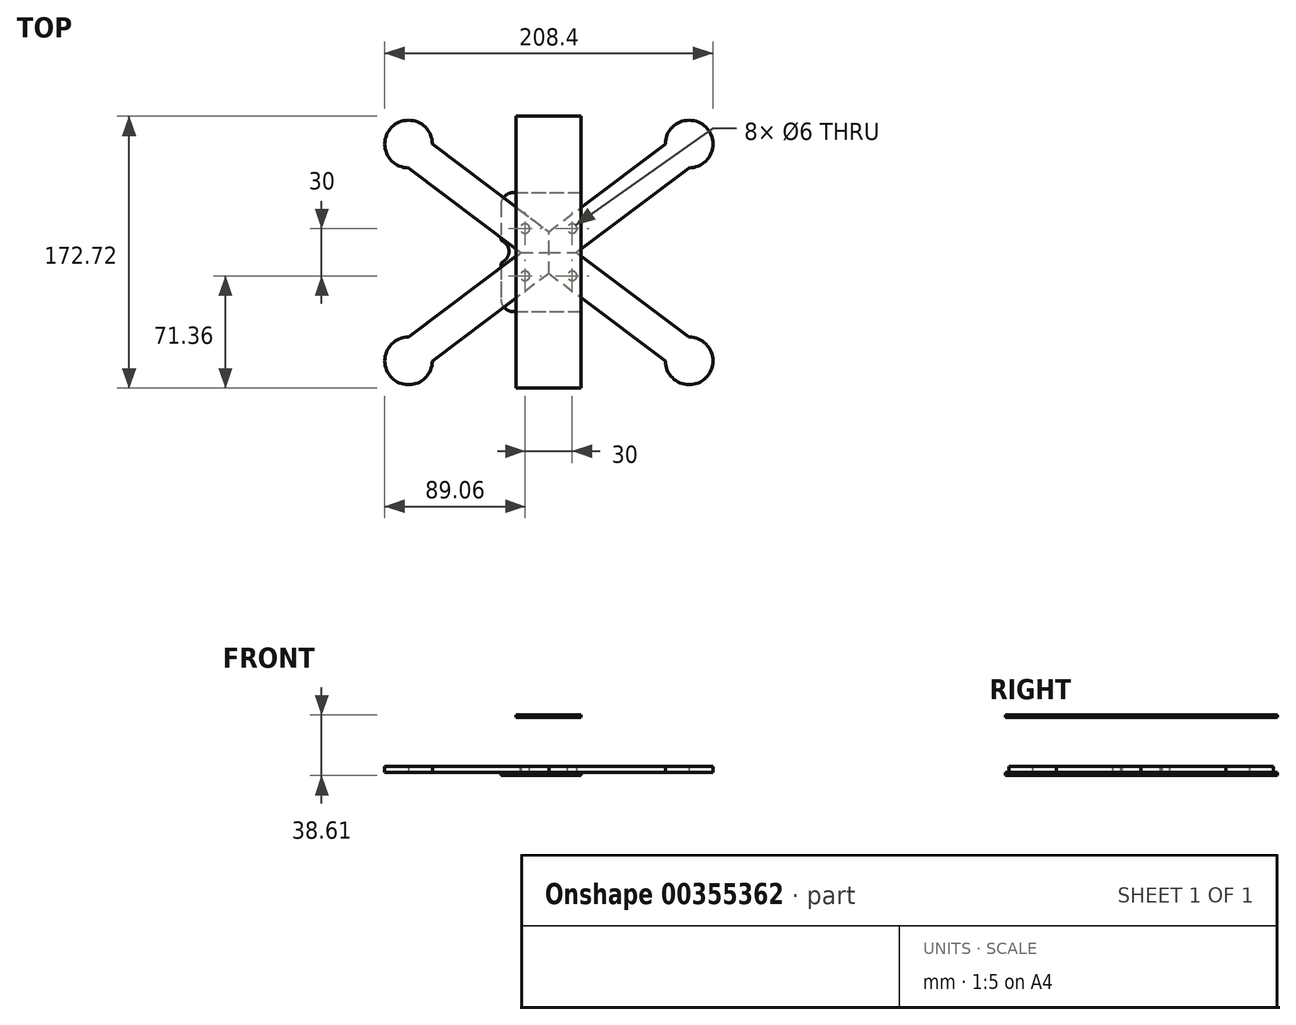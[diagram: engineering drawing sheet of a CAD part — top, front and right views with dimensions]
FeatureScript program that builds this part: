
annotation { "Feature Type Name" : "Feature", "Feature Type Description" : "" }
export const myFeature = defineFeature(function(context is Context, id is Id, definition is map)
    precondition{}
    {
        {
            var Q0;
            Q0=qCreatedBy(makeId("Top.planeOp"),FACE);
            var sketch = newSketch(context, id + "F0", { "sketchPlane" : qUnion([Q0])});
            skLineSegment(sketch, "E0.bottom", {"start": v(-20.57, 86.36) * mm, "end": v(20.58, 86.36) * mm});
            skLineSegment(sketch, "E0.top", {"start": v(-20.58, -86.36) * mm, "end": v(20.57, -86.36) * mm});
            skLineSegment(sketch, "E0.left", {"start": v(-20.57, 86.36) * mm, "end": v(-20.58, -86.36) * mm});
            skLineSegment(sketch, "E0.right", {"start": v(20.58, 86.36) * mm, "end": v(20.57, -86.36) * mm});
            skPoint(sketch, "E0.middle", {"position": v(0, 0) * mm});
            skSolve(sketch);
        }
        {
            var Q0;
            Q0 = qSketchRegion(id + "F0", true);
            var Q1;
            Q1=sQuery(id+"F0.wireOp",EDGE,"E0.left");
            var Q2;
            Q2=sQuery(id+"F0.wireOp",EDGE,"E0.top");
            var Q3;
            Q3=sQuery(id+"F0.wireOp",EDGE,"E0.right");
            var Q4;
            Q4=sQuery(id+"F0.wireOp",EDGE,"E0.bottom");
            extrude(context, id + "F1", {"entities" : qUnion([Q0]), "surfaceEntities" : qUnion([Q1, Q2, Q3, Q4]), "depth" : 2 * mm, "hasSecondDirection" : true, "secondDirectionOppositeDirection" : false, "secondDirectionDepth" : 0 * mm});
        }
        {
            var Q0;
            Q0=qCreatedBy(makeId("Top.planeOp"),FACE);
            var sketch = newSketch(context, id + "F2", { "sketchPlane" : qUnion([Q0])});
            skPoint(sketch, "E1", {"position": v(-88.95, 68.7) * mm});
            skPoint(sketch, "E2", {"position": v(-88.95, -69.06) * mm});
            skPoint(sketch, "E3", {"position": v(89.23, -69.06) * mm});
            skPoint(sketch, "E4", {"position": v(89.23, 68.7) * mm});
            skCircle(sketch, "E5", {"center": v(-88.95, 68.7) * mm, "radius": 15.11 * mm});
            skCircle(sketch, "E6", {"center": v(-88.95, -69.06) * mm, "radius": 15.11 * mm});
            skCircle(sketch, "E7", {"center": v(89.23, 68.7) * mm, "radius": 15.11 * mm});
            skCircle(sketch, "E8", {"center": v(89.23, -69.06) * mm, "radius": 15.11 * mm});
            skLineSegment(sketch, "E9", {"start": v(-88.95, 53.6) * mm, "end": v(74.12, -69.06) * mm});
            skLineSegment(sketch, "E10", {"start": v(-73.84, 68.7) * mm, "end": v(89.23, -53.95) * mm});
            skLineSegment(sketch, "E11", {"start": v(89.23, 53.6) * mm, "end": v(-73.84, -69.06) * mm});
            skLineSegment(sketch, "E12", {"start": v(-88.95, -53.95) * mm, "end": v(74.12, 68.7) * mm});
            skLineSegment(sketch, "E13", {"start": v(-17.46, -0.18) * mm, "end": v(17.74, -0.18) * mm});
            skLineSegment(sketch, "E14", {"start": v(0.14, -13.42) * mm, "end": v(0.14, 13.06) * mm});
            skSolve(sketch);
        }
        {
            var Q0;
            {var subQ0=sQuery(id+"F2.wireOp",EDGE,"E13");var subQ3=sQuery(id+"F2.wireOp",EDGE,"E14");var subQ5=makeQuery(id+"F2.imprint","INTERSECT",VERTEX,{"derivedFrom":[subQ0,subQ3]});Q0=makeQuery(id+"F2.imprint","IMPRINT",FACE,{"disambiguationData":[TD([[makeQuery(id+"F2.imprint","IMPRINT",EDGE,{"disambiguationData":[TD([[subQ5,1.0]])],"derivedFrom":subQ0}),-1.0]])]});}
            var Q1;
            {var subQ0=sQuery(id+"F2.wireOp",EDGE,"E11");var subQ1=sQuery(id+"F2.wireOp",EDGE,"E6");var subQ2=makeQuery(id+"F2.imprint","INTERSECT",VERTEX,{"derivedFrom":[subQ1,subQ0]});Q1=makeQuery(id+"F2.imprint","IMPRINT",FACE,{"disambiguationData":[TD([[makeQuery(id+"F2.imprint","IMPRINT",EDGE,{"disambiguationData":[TD([[subQ2,-1.0]])],"derivedFrom":subQ1}),-1.0]])]});}
            var Q2;
            {var subQ0=sQuery(id+"F2.wireOp",EDGE,"E6");var subQ1=makeQuery(id+"F2.imprint","INTERSECT",VERTEX,{"derivedFrom":[subQ0,sQuery(id+"F2.wireOp",EDGE,"E11")]});Q2=makeQuery(id+"F2.imprint","IMPRINT",FACE,{"disambiguationData":[TD([[makeQuery(id+"F2.imprint","IMPRINT",EDGE,{"disambiguationData":[TD([[subQ1,-1.0]])],"derivedFrom":subQ0}),1.0]])]});}
            extrude(context, id + "F3", {"entities" : qUnion([Q0, Q1, Q2]), "depth" : 6 * mm, "hasSecondDirection" : true, "secondDirectionOppositeDirection" : false, "secondDirectionDepth" : 2 * mm});
        }
        {
            var Q0;
            {var subQ0=sQuery(id+"F2.wireOp",EDGE,"E8");var subQ1=makeQuery(id+"F2.imprint","INTERSECT",VERTEX,{"derivedFrom":[subQ0,sQuery(id+"F2.wireOp",EDGE,"E9")]});Q0=makeQuery(id+"F2.imprint","IMPRINT",FACE,{"disambiguationData":[TD([[makeQuery(id+"F2.imprint","IMPRINT",EDGE,{"disambiguationData":[TD([[subQ1,1.0]])],"derivedFrom":subQ0}),1.0]])]});}
            var Q1;
            {var subQ0=sQuery(id+"F2.wireOp",EDGE,"E9");var subQ1=sQuery(id+"F2.wireOp",EDGE,"E8");var subQ2=makeQuery(id+"F2.imprint","INTERSECT",VERTEX,{"derivedFrom":[subQ1,subQ0]});Q1=makeQuery(id+"F2.imprint","IMPRINT",FACE,{"disambiguationData":[TD([[makeQuery(id+"F2.imprint","IMPRINT",EDGE,{"disambiguationData":[TD([[subQ2,1.0]])],"derivedFrom":subQ1}),-1.0]])]});}
            var Q2;
            {var subQ0=sQuery(id+"F2.wireOp",EDGE,"E13");var subQ3=sQuery(id+"F2.wireOp",EDGE,"E14");var subQ5=makeQuery(id+"F2.imprint","INTERSECT",VERTEX,{"derivedFrom":[subQ0,subQ3]});Q2=makeQuery(id+"F2.imprint","IMPRINT",FACE,{"disambiguationData":[TD([[makeQuery(id+"F2.imprint","IMPRINT",EDGE,{"disambiguationData":[TD([[subQ5,-1.0]])],"derivedFrom":subQ0}),-1.0]])]});}
            extrude(context, id + "F4", {"entities" : qUnion([Q0, Q1, Q2]), "depth" : 6 * mm, "hasSecondDirection" : true, "secondDirectionOppositeDirection" : false, "secondDirectionDepth" : 2 * mm});
        }
        {
            var Q0;
            {var subQ0=sQuery(id+"F2.wireOp",EDGE,"E7");var subQ1=makeQuery(id+"F2.imprint","INTERSECT",VERTEX,{"derivedFrom":[subQ0,sQuery(id+"F2.wireOp",EDGE,"E11")]});Q0=makeQuery(id+"F2.imprint","IMPRINT",FACE,{"disambiguationData":[TD([[makeQuery(id+"F2.imprint","IMPRINT",EDGE,{"disambiguationData":[TD([[subQ1,1.0]])],"derivedFrom":subQ0}),1.0]])]});}
            var Q1;
            {var subQ0=sQuery(id+"F2.wireOp",EDGE,"E11");var subQ1=sQuery(id+"F2.wireOp",EDGE,"E7");var subQ2=makeQuery(id+"F2.imprint","INTERSECT",VERTEX,{"derivedFrom":[subQ1,subQ0]});Q1=makeQuery(id+"F2.imprint","IMPRINT",FACE,{"disambiguationData":[TD([[makeQuery(id+"F2.imprint","IMPRINT",EDGE,{"disambiguationData":[TD([[subQ2,1.0]])],"derivedFrom":subQ1}),-1.0]])]});}
            var Q2;
            {var subQ0=sQuery(id+"F2.wireOp",EDGE,"E13");var subQ3=sQuery(id+"F2.wireOp",EDGE,"E14");var subQ5=makeQuery(id+"F2.imprint","INTERSECT",VERTEX,{"derivedFrom":[subQ0,subQ3]});Q2=makeQuery(id+"F2.imprint","IMPRINT",FACE,{"disambiguationData":[TD([[makeQuery(id+"F2.imprint","IMPRINT",EDGE,{"disambiguationData":[TD([[subQ5,-1.0]])],"derivedFrom":subQ0}),1.0]])]});}
            extrude(context, id + "F5", {"entities" : qUnion([Q0, Q1, Q2]), "depth" : 6 * mm, "hasSecondDirection" : true, "secondDirectionOppositeDirection" : false, "secondDirectionDepth" : 2 * mm});
        }
        {
            var Q0;
            {var subQ0=sQuery(id+"F2.wireOp",EDGE,"E5");var subQ1=makeQuery(id+"F2.imprint","INTERSECT",VERTEX,{"derivedFrom":[subQ0,sQuery(id+"F2.wireOp",EDGE,"E9")]});Q0=makeQuery(id+"F2.imprint","IMPRINT",FACE,{"disambiguationData":[TD([[makeQuery(id+"F2.imprint","IMPRINT",EDGE,{"disambiguationData":[TD([[subQ1,1.0]])],"derivedFrom":subQ0}),1.0]])]});}
            var Q1;
            {var subQ0=sQuery(id+"F2.wireOp",EDGE,"E9");var subQ1=sQuery(id+"F2.wireOp",EDGE,"E5");var subQ2=makeQuery(id+"F2.imprint","INTERSECT",VERTEX,{"derivedFrom":[subQ1,subQ0]});Q1=makeQuery(id+"F2.imprint","IMPRINT",FACE,{"disambiguationData":[TD([[makeQuery(id+"F2.imprint","IMPRINT",EDGE,{"disambiguationData":[TD([[subQ2,-1.0]])],"derivedFrom":subQ1}),-1.0]])]});}
            var Q2;
            {var subQ0=sQuery(id+"F2.wireOp",EDGE,"E13");var subQ3=sQuery(id+"F2.wireOp",EDGE,"E14");var subQ5=makeQuery(id+"F2.imprint","INTERSECT",VERTEX,{"derivedFrom":[subQ0,subQ3]});Q2=makeQuery(id+"F2.imprint","IMPRINT",FACE,{"disambiguationData":[TD([[makeQuery(id+"F2.imprint","IMPRINT",EDGE,{"disambiguationData":[TD([[subQ5,1.0]])],"derivedFrom":subQ0}),1.0]])]});}
            extrude(context, id + "F6", {"entities" : qUnion([Q0, Q1, Q2]), "depth" : 6 * mm, "hasSecondDirection" : true, "secondDirectionOppositeDirection" : false, "secondDirectionDepth" : 2 * mm});
        }
        {
            var Q0;
            Q0=qCreatedBy(makeId("Top.planeOp"),FACE);
            var sketch = newSketch(context, id + "F7", { "sketchPlane" : qUnion([Q0])});
            skLineSegment(sketch, "E15.bottom", {"start": v(-20.57, 86.36) * mm, "end": v(20.58, 86.36) * mm});
            skLineSegment(sketch, "E15.top", {"start": v(-20.58, -86.36) * mm, "end": v(20.57, -86.36) * mm});
            skLineSegment(sketch, "E15.left", {"start": v(-20.57, 86.36) * mm, "end": v(-20.58, -86.36) * mm});
            skLineSegment(sketch, "E15.right", {"start": v(20.58, 86.36) * mm, "end": v(20.57, -86.36) * mm});
            skPoint(sketch, "E15.middle", {"position": v(0, 0) * mm});
            skSolve(sketch);
        }
        {
            var Q0;
            Q0 = qSketchRegion(id + "F7", true);
            extrude(context, id + "F8", {"entities" : qUnion([Q0]), "depth" : 38.6 * mm, "hasSecondDirection" : true, "secondDirectionOppositeDirection" : false, "secondDirectionDepth" : 37.1 * mm});
        }
        {
            var Q0;
            Q0=makeQuery(id+"F0.imprint","IMPRINT",FACE,{"disambiguationData":[TD([[makeQuery(id+"F0.imprint","IMPRINT",EDGE,{"derivedFrom":sQuery(id+"F0.wireOp",EDGE,"E0.bottom")}),-1.0]])]});
            var sketch = newSketch(context, id + "F9", { "sketchPlane" : qUnion([Q0])});
            skLineSegment(sketch, "E16.bottom", {"start": v(15, 15) * mm, "end": v(-15, 15) * mm, "construction": true});
            skLineSegment(sketch, "E16.top", {"start": v(15, -15) * mm, "end": v(-15, -15) * mm, "construction": true});
            skLineSegment(sketch, "E16.left", {"start": v(15, 15) * mm, "end": v(15, -15) * mm, "construction": true});
            skLineSegment(sketch, "E16.right", {"start": v(-15, 15) * mm, "end": v(-15, -15) * mm, "construction": true});
            skPoint(sketch, "E16.middle", {"position": v(0, 0) * mm});
            skCircle(sketch, "E17", {"center": v(15, 15) * mm, "radius": 3 * mm});
            skCircle(sketch, "E18", {"center": v(15, -15) * mm, "radius": 3 * mm});
            skCircle(sketch, "E19", {"center": v(-15, -15) * mm, "radius": 3 * mm});
            skCircle(sketch, "E20", {"center": v(-15, 15) * mm, "radius": 3 * mm});
            skSolve(sketch);
        }
        {
            var Q0;
            Q0 = qSketchRegion(id + "F9", true);
            extrude(context, id + "F10", {"entities" : qUnion([Q0]), "operationType" : NewBodyOperationType.REMOVE, "oppositeDirection" : true, "depth" : 2 * mm, "hasSecondDirection" : true, "secondDirectionOppositeDirection" : false, "secondDirectionDepth" : 8 * mm});
        }
        {
            var Q0;
            Q0=makeQuery(id+"F7.imprint","IMPRINT",FACE,{"disambiguationData":[TD([[makeQuery(id+"F7.imprint","IMPRINT",EDGE,{"derivedFrom":sQuery(id+"F7.wireOp",EDGE,"E15.bottom")}),-1.0]])]});
            var sketch = newSketch(context, id + "F11", { "sketchPlane" : qUnion([Q0])});
            skLineSegment(sketch, "E21.bottom", {"start": v(-22.3, 37.89) * mm, "end": v(22.4, 37.89) * mm});
            skLineSegment(sketch, "E21.top", {"start": v(-22.3, -37.78) * mm, "end": v(22.4, -37.78) * mm});
            skLineSegment(sketch, "E21.left", {"start": v(-30.3, 29.89) * mm, "end": v(-30.3, -29.78) * mm});
            skLineSegment(sketch, "E21.right", {"start": v(30.4, 29.89) * mm, "end": v(30.4, -29.78) * mm});
            skPoint(sketch, "E21.middle", {"position": v(0.04, 1.1) * mm});
            skLineSegment(sketch, "E22", {"start": v(-30.3, -7.27) * mm, "end": v(-27.5, -4.75) * mm});
            skLineSegment(sketch, "E23", {"start": v(-30.3, 7.73) * mm, "end": v(-28.11, 6.17) * mm});
            skLineSegment(sketch, "E24", {"start": v(30.4, -7.27) * mm, "end": v(27.59, -4.9) * mm});
            skLineSegment(sketch, "E25", {"start": v(30.4, 7.73) * mm, "end": v(28.2, 6.27) * mm});
            skPoint(sketch, "E26.visualSharp", {"position": v(-20.95, 1.1) * mm});
            skArc(sketch, "E26.filletArc", {"start": v(-27.5, -4.75) * mm, "mid": v(-25.17, 0.86) * mm, "end": v(-28.11, 6.17) * mm});
            skPoint(sketch, "E27.visualSharp", {"position": v(20.44, 1.1) * mm});
            skArc(sketch, "E27.filletArc", {"start": v(28.2, 6.27) * mm, "mid": v(25.1, 0.84) * mm, "end": v(27.59, -4.9) * mm});
            skPoint(sketch, "E28.visualSharp", {"position": v(-30.3, 37.89) * mm});
            skArc(sketch, "E28.filletArc", {"start": v(-22.3, 37.89) * mm, "mid": v(-27.96, 35.54) * mm, "end": v(-30.3, 29.89) * mm});
            skPoint(sketch, "E29.visualSharp", {"position": v(30.4, 37.89) * mm});
            skArc(sketch, "E29.filletArc", {"start": v(30.4, 29.89) * mm, "mid": v(28.05, 35.54) * mm, "end": v(22.4, 37.89) * mm});
            skPoint(sketch, "E30.visualSharp", {"position": v(30.4, -37.78) * mm});
            skArc(sketch, "E30.filletArc", {"start": v(22.4, -37.78) * mm, "mid": v(28.05, -35.44) * mm, "end": v(30.4, -29.78) * mm});
            skPoint(sketch, "E31.visualSharp", {"position": v(-30.3, -37.78) * mm});
            skArc(sketch, "E31.filletArc", {"start": v(-30.3, -29.78) * mm, "mid": v(-27.96, -35.44) * mm, "end": v(-22.3, -37.78) * mm});
            skSolve(sketch);
        }
        {
            var Q0;
            {var subQ0=sQuery(id+"F11.wireOp",EDGE,"13fc5a92-0e27-4795-82d0-adb177627d8e.filletArc");var subQ1=sQuery(id+"F11.wireOp",EDGE,"E21.left");var subQ2=makeQuery(id+"F11.imprint","INTERSECT",VERTEX,{"derivedFrom":[subQ1,subQ0]});Q0=makeQuery(id+"F11.imprint","IMPRINT",FACE,{"disambiguationData":[TD([[makeQuery(id+"F11.imprint","IMPRINT",EDGE,{"disambiguationData":[TD([[subQ2,-1.0]])],"derivedFrom":subQ1}),1.0]])]});}
            var Q1;
            {var subQ0=sQuery(id+"F11.wireOp",EDGE,"1b451bdf-7777-4f3a-bd97-647accafad0b.filletArc");var subQ1=sQuery(id+"F11.wireOp",EDGE,"E21.left");var subQ2=makeQuery(id+"F11.imprint","INTERSECT",VERTEX,{"derivedFrom":[subQ1,subQ0]});Q1=makeQuery(id+"F11.imprint","IMPRINT",FACE,{"disambiguationData":[TD([[makeQuery(id+"F11.imprint","IMPRINT",EDGE,{"disambiguationData":[TD([[subQ2,1.0]])],"derivedFrom":subQ1}),1.0]])]});}
            var Q2;
            {var subQ1=sQuery(id+"F11.wireOp",EDGE,"2e5d9f3c-c106-46cf-a738-4a28743fc0ae.filletArc");Q2=makeQuery(id+"F11.imprint","IMPRINT",FACE,{"disambiguationData":[TD([[makeQuery(id+"F11.imprint","IMPRINT",EDGE,{"derivedFrom":subQ1}),1.0]])]});}
            var Q3;
            {var subQ1=sQuery(id+"F11.wireOp",EDGE,"E21.bottom");Q3=makeQuery(id+"F11.imprint","IMPRINT",FACE,{"disambiguationData":[TD([[makeQuery(id+"F11.imprint","IMPRINT",EDGE,{"derivedFrom":subQ1}),-1.0]])]});}
            var Q4;
            Q4=makeQuery(id+"F0.imprint","IMPRINT",FACE,{"disambiguationData":[TD([[makeQuery(id+"F0.imprint","IMPRINT",EDGE,{"derivedFrom":sQuery(id+"F0.wireOp",EDGE,"E0.bottom")}),-1.0]])]});
            extrude(context, id + "F12", {"entities" : qUnion([Q0, Q1, Q2, Q3, Q4]), "depth" : 2 * mm});
        }
    });
